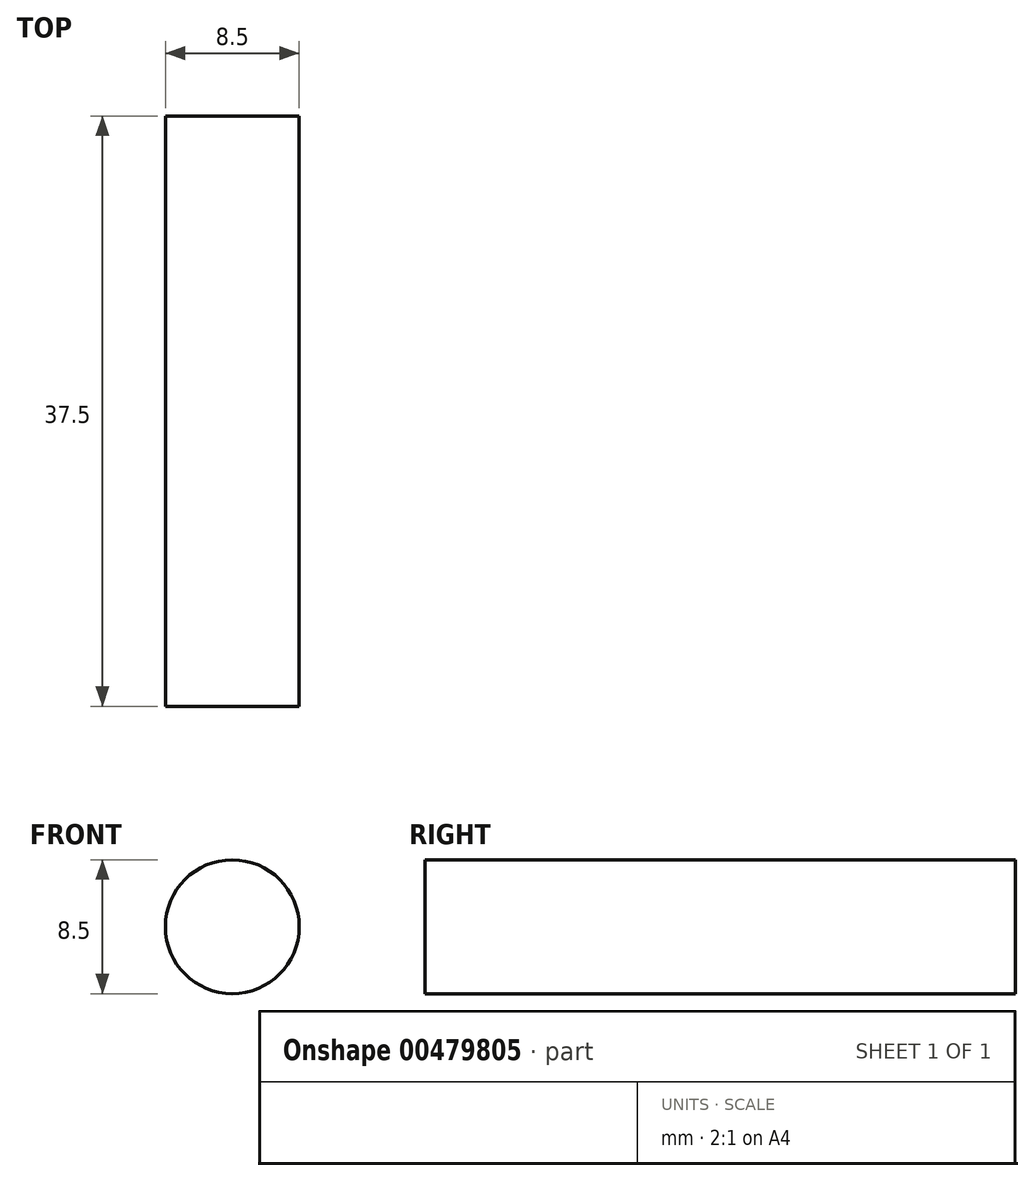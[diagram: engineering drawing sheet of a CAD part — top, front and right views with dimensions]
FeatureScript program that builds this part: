
annotation { "Feature Type Name" : "Feature", "Feature Type Description" : "" }
export const myFeature = defineFeature(function(context is Context, id is Id, definition is map)
    precondition{}
    {
        {
            var Q0;
            Q0=qCreatedBy(makeId("Front.planeOp"),FACE);
            var sketch = newSketch(context, id + "F0", { "sketchPlane" : qUnion([Q0])});
            skCircle(sketch, "E0", {"center": v(0, 0) * mm, "radius": 4.25 * mm});
            skSolve(sketch);
        }
        {
            var Q0;
            Q0=makeQuery(id+"F0.imprint","IMPRINT",FACE,{"disambiguationData":[TD([[makeQuery(id+"F0.imprint","IMPRINT",EDGE,{"derivedFrom":sQuery(id+"F0.wireOp",EDGE,"E0")}),1.0]])]});
            var Q1;
            Q1=sQuery(id+"F0.wireOp",EDGE,"E0");
            extrude(context, id + "F1", {"entities" : qUnion([Q0]), "surfaceEntities" : qUnion([Q1]), "depth" : 37.5 * mm});
        }
    });
